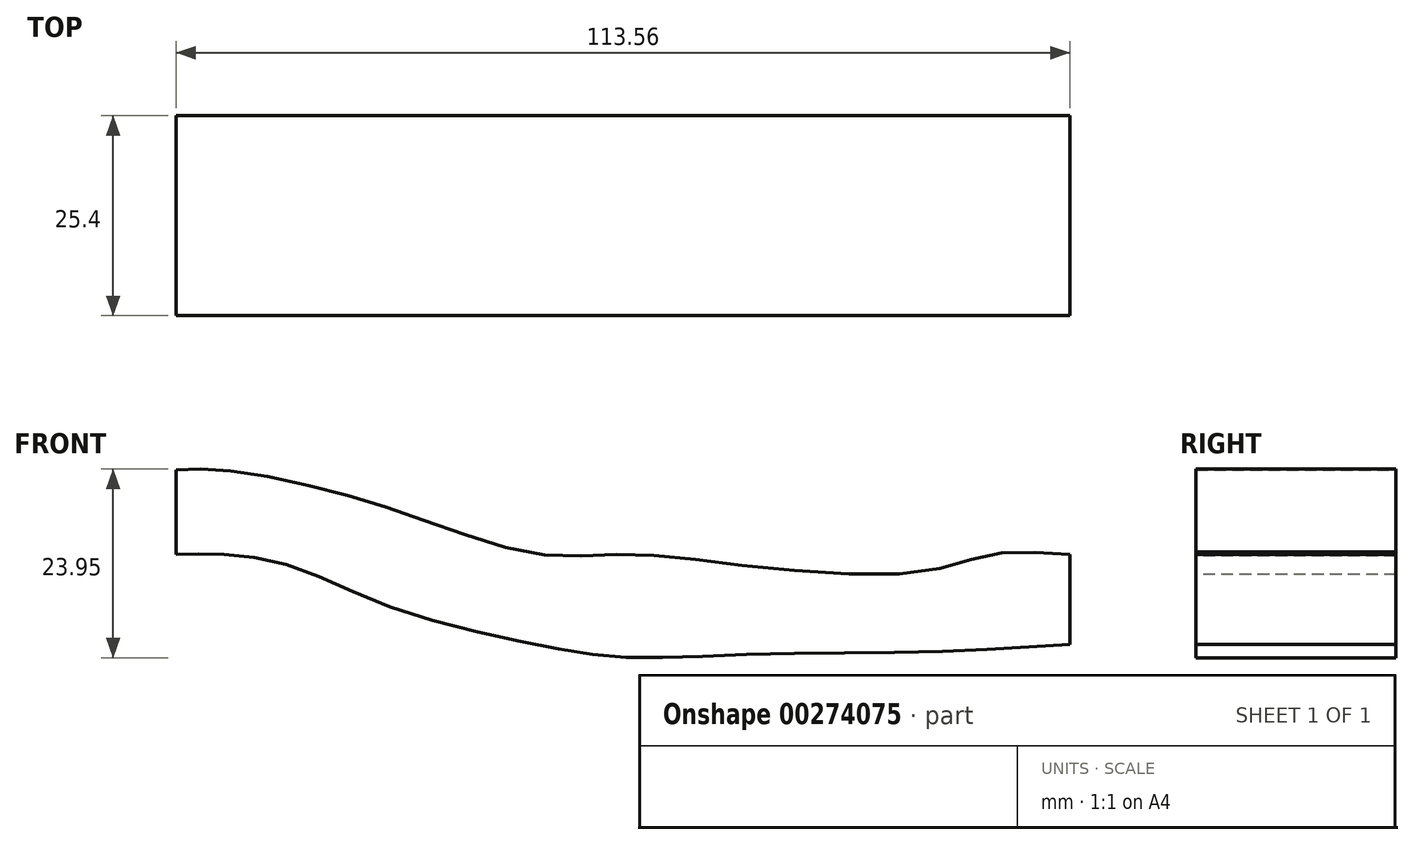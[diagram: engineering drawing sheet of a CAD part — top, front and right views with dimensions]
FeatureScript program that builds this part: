
annotation { "Feature Type Name" : "Feature", "Feature Type Description" : "" }
export const myFeature = defineFeature(function(context is Context, id is Id, definition is map)
    precondition{}
    {
        {
            var Q0;
            Q0=qCreatedBy(makeId("Front.planeOp"),FACE);
            var sketch = newSketch(context, id + "F0", { "sketchPlane" : qUnion([Q0])});
            skLineSegment(sketch, "E0", {"start": v(-57.15, 0) * mm, "end": v(-57.15, 10.7) * mm});
            skLineSegment(sketch, "E1", {"start": v(56.41, 0) * mm, "end": v(56.41, -11.43) * mm});
            skFitSpline(sketch, "E2", {"points": [v(-57.15, 10.7) * mm, v(-51.25, 10.7) * mm, v(-38.53, 8.3) * mm, v(-25.44, 4.24) * mm, v(-11.06, 0) * mm, v(0, 0) * mm, v(15.49, -1.47) * mm, v(37.6, -2.21) * mm, v(46.64, 0) * mm, v(56.41, 0) * mm], "startDerivative": vector(69.28, 4) * mm, "endDerivative": vector(104.13, -7.56) * mm});
            skFitSpline(sketch, "E3", {"points": [v(-57.15, 0) * mm, v(-51.8, 0) * mm, v(-42.59, -1.47) * mm, v(-30.05, -6.64) * mm, v(-11.61, -11.43) * mm, v(0, -13.09) * mm, v(15.49, -12.72) * mm, v(38.71, -12.35) * mm, v(56.41, -11.43) * mm], "startDerivative": vector(64.25, 1.72) * mm, "endDerivative": vector(119.2, 7.93) * mm});
            skSolve(sketch);
        }
        {
            var Q0;
            Q0=makeQuery(id+"F0.imprint","IMPRINT",FACE,{"disambiguationData":[TD([[makeQuery(id+"F0.imprint","IMPRINT",EDGE,{"derivedFrom":sQuery(id+"F0.wireOp",EDGE,"E0")}),-1.0]])]});
            extrude(context, id + "F1", {"entities" : qUnion([Q0]), "depth" : 25.4 * mm});
        }
    });
